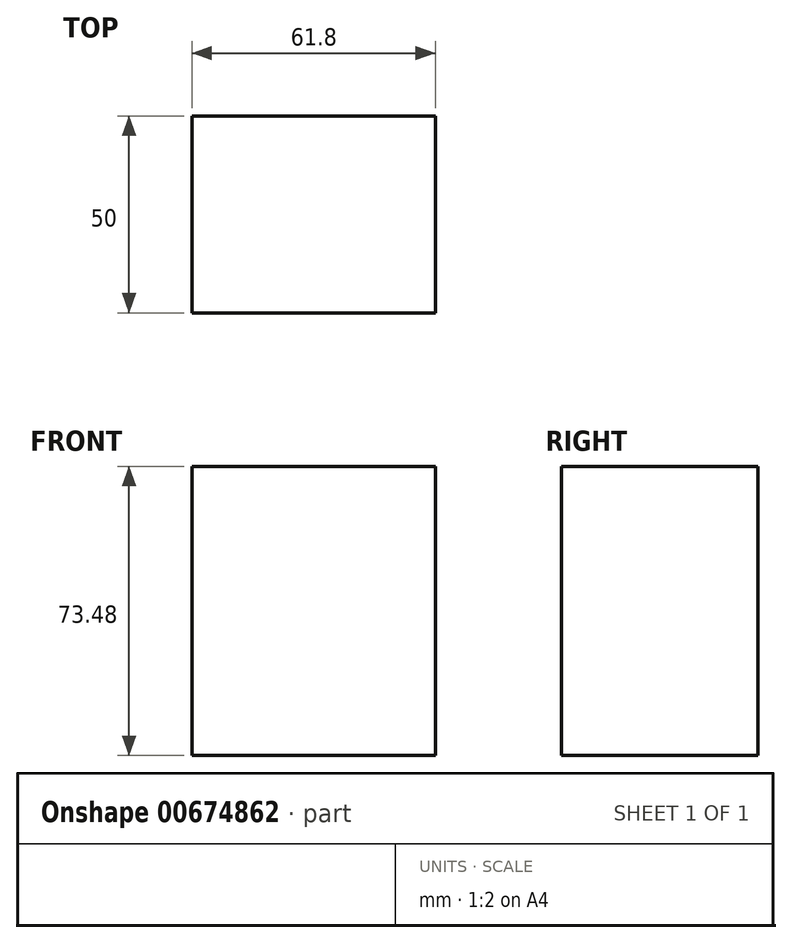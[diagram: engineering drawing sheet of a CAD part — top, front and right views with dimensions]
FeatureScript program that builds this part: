
annotation { "Feature Type Name" : "Feature", "Feature Type Description" : "" }
export const myFeature = defineFeature(function(context is Context, id is Id, definition is map)
    precondition{}
    {
        {
            var Q0;
            Q0=qCreatedBy(makeId("Front.planeOp"),FACE);
            var sketch = newSketch(context, id + "F0", { "sketchPlane" : qUnion([Q0])});
            skLineSegment(sketch, "E0.bottom", {"start": v(30.9, 36.74) * mm, "end": v(-30.9, 36.74) * mm});
            skLineSegment(sketch, "E0.top", {"start": v(30.9, -36.74) * mm, "end": v(-30.9, -36.74) * mm});
            skLineSegment(sketch, "E0.left", {"start": v(30.9, 36.74) * mm, "end": v(30.9, -36.74) * mm});
            skLineSegment(sketch, "E0.right", {"start": v(-30.9, 36.74) * mm, "end": v(-30.9, -36.74) * mm});
            skPoint(sketch, "E0.middle", {"position": v(0, 0) * mm});
            skSolve(sketch);
        }
        {
            var Q0;
            Q0=makeQuery(id+"F0.imprint","IMPRINT",FACE,{"disambiguationData":[TD([[makeQuery(id+"F0.imprint","IMPRINT",EDGE,{"derivedFrom":sQuery(id+"F0.wireOp",EDGE,"E0.bottom")}),1.0]])]});
            extrude(context, id + "F1", {"entities" : qUnion([Q0]), "depth" : 50 * mm, "offsetDistance" : 25 * mm});
        }
    });
